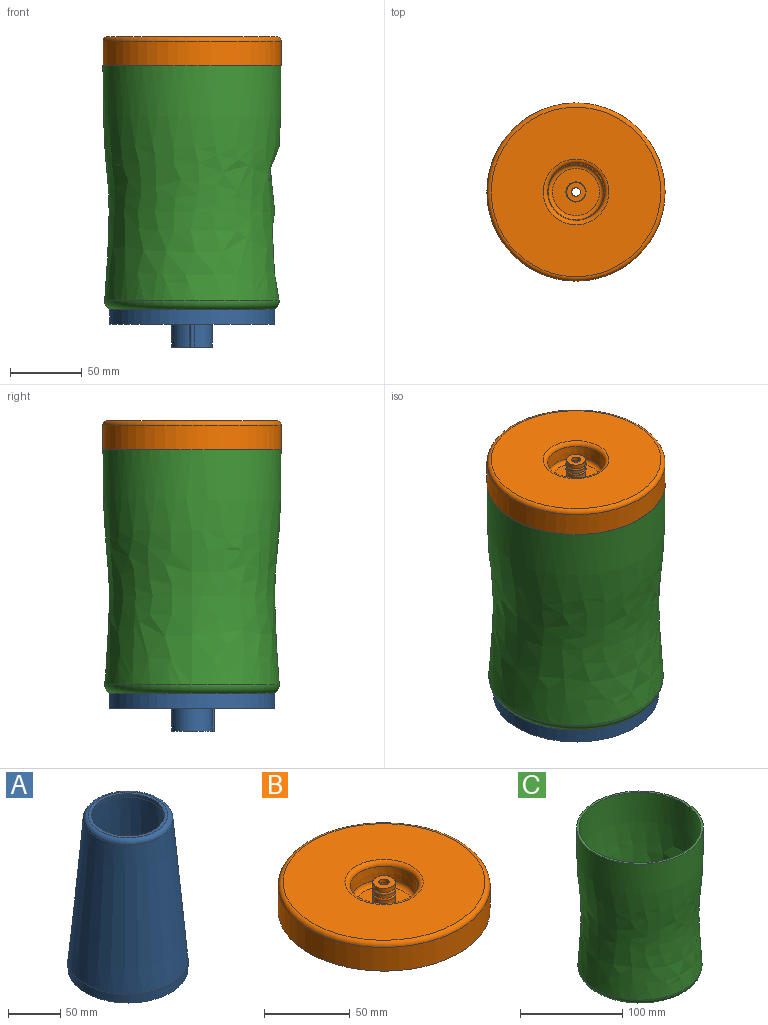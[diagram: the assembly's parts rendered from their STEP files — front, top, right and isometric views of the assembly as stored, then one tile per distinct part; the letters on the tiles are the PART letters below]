
ASSEMBLY  parts=3 mates=2
PART A: 15 faces, bbox 115x115x196 mm
  f0: plane 106.97x106.97mm, normal (0,0,1), area 8953.7mm2, adj f3,f12
  f1: plane 8x8mm, normal (0,0,-1), area 17.1mm2, adj f3,f6
  f2: cylinder r=57.5mm len=115mm, axis (0,0,-1), area 3612.8mm2, adj f4,f13
  f3: cylinder r=3.25mm len=10mm, axis (0,0,-1), area 204.2mm2, adj f0,f1
  f4: plane 115x115mm, normal (0,0,-1), area 9749.8mm2, adj f2,f5,f7
  f5: cylinder r=1.5mm len=16mm, axis (0,0,1), area 77.9mm2, adj f4,f7,f8
  f6: cylinder r=4mm len=16mm, axis (0,0,1), area 402.1mm2, adj f1,f8
  f7: cylinder r=14.2mm len=28.4mm, axis (0,0,1), area 1379.5mm2, adj f4,f5,f8
  f8: plane 29.9x28.4mm, normal (0,0,-1), area 586.8mm2, adj f5,f6,f7
  f9: plane 76.09x76.09mm, normal (0,0,1), area 698.8mm2, adj f10,f14
  f10: cylinder r=35mm len=70mm, axis (0,0,-1), area 879.6mm2, adj f9,f11
  f11: plane 77.92x77.92mm, normal (0,0,-1), area 920.5mm2, adj f10,f12
  f12: cone r=53.48mm half-angle=5deg, axis (0,0,-1), area 48395.3mm2, adj f0,f11
  f13: cone r=42.63mm half-angle=5deg, axis (0,0,-1), area 52446.3mm2, adj f2,f14
  f14: torus R=38.05mm, axis (0,0,-1), area 1916.5mm2, adj f9,f13
PART B: 24 faces, bbox 134.2x134.2x20 mm
  f0: cylinder r=6.55mm len=13.1mm, axis (0,0,1), area 253.7mm2, adj f7,f23
  f1: cylinder r=6.55mm len=13.1mm, axis (0,0,1), area 95.9mm2, adj f22,f23
  f2: cylinder r=62mm len=124mm, axis (0,0,-1), area 6622.5mm2, adj f4,f11
  f3: plane 118x118mm, normal (0,0,1), area 9296mm2, adj f9,f11
  f4: plane 124x124mm, normal (0,0,-1), area 954.3mm2, adj f2,f12
  f5: cylinder r=6.55mm len=13.1mm, axis (0,0,1), area 130.2mm2, adj f8,f22
  f6: cone r=20mm half-angle=3deg, axis (0,0,1), area 1149mm2, adj f9,f10
  f7: plane 32.73x32.73mm, normal (0,0,1), area 706.8mm2, adj f0,f10
  f8: plane 13.1x13.1mm, normal (0,0,1), area 106.5mm2, adj f5,f21
  f9: torus R=22.85mm, axis (0,0,1), area 600.3mm2, adj f3,f6
  f10: torus R=16.37mm, axis (0,0,1), area 522mm2, adj f6,f7
  f11: torus R=59mm, axis (0,0,1), area 1803.5mm2, adj f2,f3
  f12: cylinder r=59.5mm len=119mm, axis (0,0,-1), area 6355.4mm2, adj f4,f20
  f13: plane 118x118mm, normal (0,0,-1), area 9296mm2, adj f18,f20
  f14: cylinder r=4.05mm len=15mm, axis (0,0,1), area 381.7mm2, adj f16,f17
  f15: cone r=22.5mm half-angle=3deg, axis (0,0,1), area 1295.3mm2, adj f18,f19
  f16: plane 32.73x32.73mm, normal (0,0,-1), area 790mm2, adj f14,f19
  f17: plane 8.1x8.1mm, normal (0,0,-1), area 23.3mm2, adj f14,f21
  f18: torus R=22.85mm, axis (0,0,1), area 107.5mm2, adj f13,f15
  f19: torus R=16.37mm, axis (0,0,1), area 1039mm2, adj f15,f16
  f20: torus R=59mm, axis (0,0,1), area 292.7mm2, adj f12,f13
  f21: cylinder r=3mm len=6mm, axis (0,0,1), area 47.1mm2, adj f8,f17
  f22: torus R=6mm, axis (0,0,-1), area 85mm2, adj f1,f5
  f23: torus R=6mm, axis (0,0,-1), area 85mm2, adj f0,f1
PART C: 6 faces, bbox 131.5x131.5x170 mm
  f0: revolved ~163.59x124mm, area 61606.6mm2, adj f1,f2
  f1: plane 124x124mm, normal (0,0,1), area 954.3mm2, adj f0,f4
  f2: torus R=54.75mm, axis (0,0,-1), area 6479.8mm2, adj f0,f3
  f3: plane 102.58x102.58mm, normal (0,0,1), area 791.1mm2, adj f2,f5
  f4: revolved ~163.76x119mm, area 59093.3mm2, adj f1,f5
  f5: torus R=54.75mm, axis (0,0,-1), area 3700.7mm2, adj f3,f4
PLACE A t=(0.16,-0.13,-2.34)mm fixed
PLACE B t=(0.16,-0.13,177.66)mm
PLACE C t=(0.16,-0.13,-96.6)mm
MATE fastened C.f2 <-> B.f2  axis (0,0,1) through (0.16,-0.13,177.66)mm
MATE slider A.f7 <-> B.f2  axis (0,0,-1) through (0.16,-0.13,-2.34)mm
